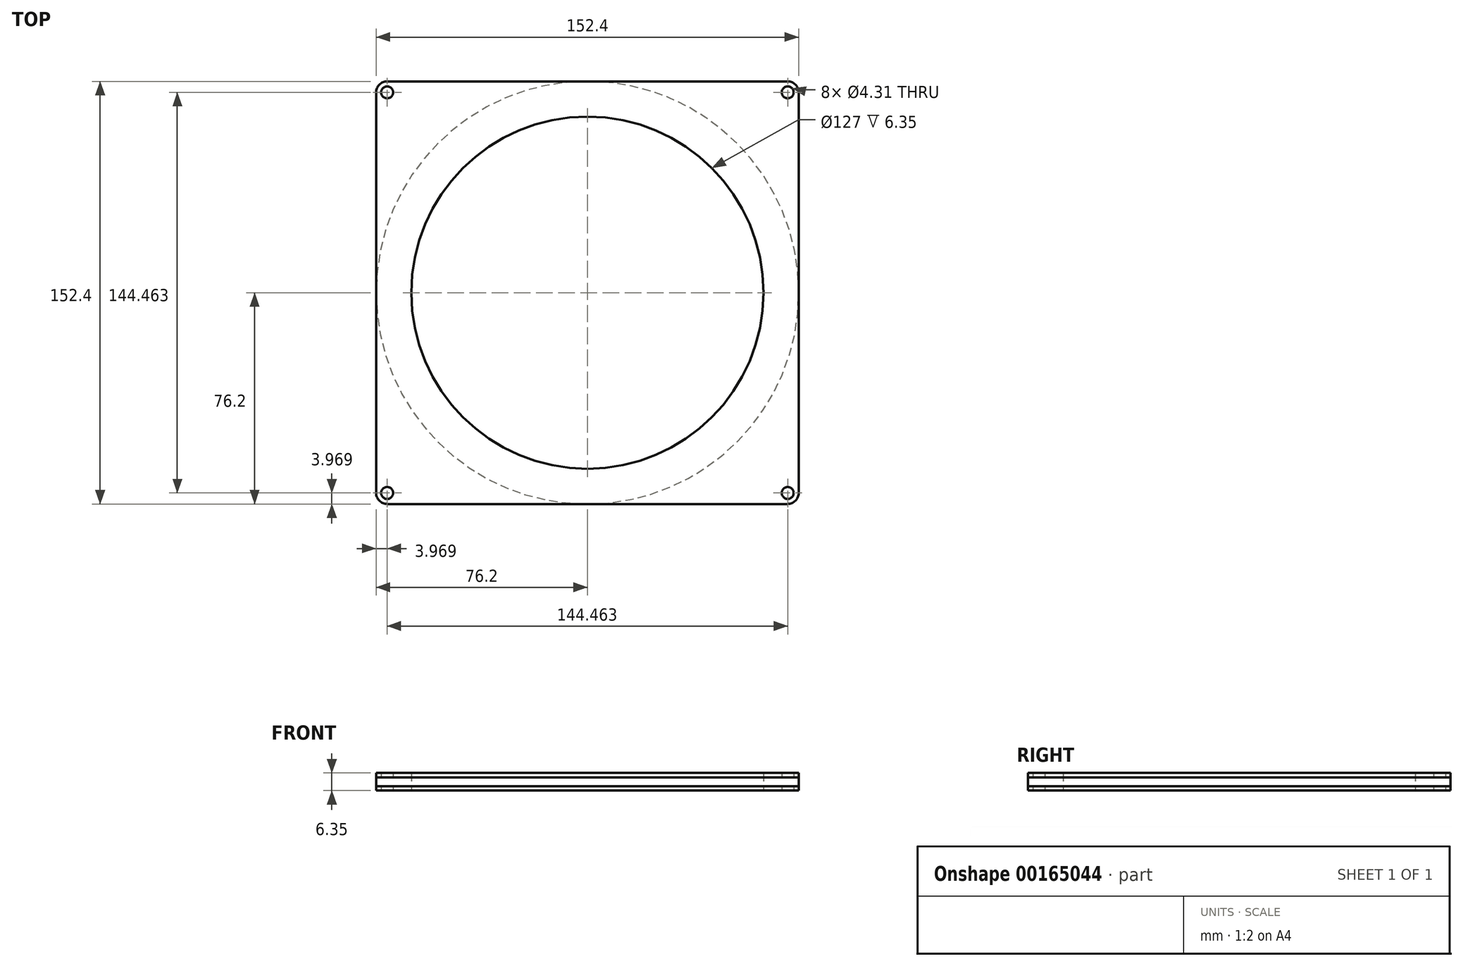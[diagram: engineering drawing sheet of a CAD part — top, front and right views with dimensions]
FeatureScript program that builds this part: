
annotation { "Feature Type Name" : "Feature", "Feature Type Description" : "" }
export const myFeature = defineFeature(function(context is Context, id is Id, definition is map)
    precondition{}
    {
        {
            var Q0;
            Q0=qCreatedBy(makeId("Top.planeOp"),FACE);
            var sketch = newSketch(context, id + "F0", { "sketchPlane" : qUnion([Q0])});
            skLineSegment(sketch, "E0.bottom", {"start": v(76.2, 76.2) * mm, "end": v(-76.2, 76.2) * mm});
            skLineSegment(sketch, "E0.top", {"start": v(76.2, -76.2) * mm, "end": v(-76.2, -76.2) * mm});
            skLineSegment(sketch, "E0.left", {"start": v(76.2, 76.2) * mm, "end": v(76.2, -76.2) * mm});
            skLineSegment(sketch, "E0.right", {"start": v(-76.2, 76.2) * mm, "end": v(-76.2, -76.2) * mm});
            skPoint(sketch, "E0.middle", {"position": v(0, 0) * mm});
            skLineSegment(sketch, "E1.bottom", {"start": v(-72.23, 72.23) * mm, "end": v(72.23, 72.23) * mm, "construction": true});
            skLineSegment(sketch, "E1.top", {"start": v(-72.23, -72.23) * mm, "end": v(72.23, -72.23) * mm, "construction": true});
            skLineSegment(sketch, "E1.left", {"start": v(-72.23, 72.23) * mm, "end": v(-72.23, -72.23) * mm, "construction": true});
            skLineSegment(sketch, "E1.right", {"start": v(72.23, 72.23) * mm, "end": v(72.23, -72.23) * mm, "construction": true});
            skLineSegment(sketch, "E2", {"start": v(0, 72.23) * mm, "end": v(0, 76.2) * mm, "construction": true});
            skCircle(sketch, "E3", {"center": v(-72.23, 72.23) * mm, "radius": 2.15 * mm});
            skCircle(sketch, "E4", {"center": v(72.23, 72.23) * mm, "radius": 2.15 * mm});
            skCircle(sketch, "E5", {"center": v(72.23, -72.23) * mm, "radius": 2.15 * mm});
            skCircle(sketch, "E6", {"center": v(-72.23, -72.23) * mm, "radius": 2.15 * mm});
            skCircle(sketch, "E7", {"center": v(0, 0) * mm, "radius": 63.5 * mm});
            skSolve(sketch);
        }
        {
            var Q0;
            Q0 = qSketchRegion(id + "F0", true);
            extrude(context, id + "F1", {"entities" : qUnion([Q0]), "depth" : 1.59 * mm});
        }
        {
            var Q0;
            Q0=makeQuery(id+"F1.opExtrude","CAP_FACE",FACE,{"disambiguationData":[OSD([sQuery(id+"F0.wireOp",EDGE,"E0.bottom"),sQuery(id+"F0.wireOp",EDGE,"E0.top"),sQuery(id+"F0.wireOp",EDGE,"E0.left"),sQuery(id+"F0.wireOp",EDGE,"E0.right"),sQuery(id+"F0.wireOp",EDGE,"E3"),sQuery(id+"F0.wireOp",EDGE,"E4"),sQuery(id+"F0.wireOp",EDGE,"E5"),sQuery(id+"F0.wireOp",EDGE,"E6")])],"isStart":false});
            var sketch = newSketch(context, id + "F2", { "sketchPlane" : qUnion([Q0])});
            skCircle(sketch, "E8", {"center": v(0, 0) * mm, "radius": 76.2 * mm});
            skCircle(sketch, "E9", {"center": v(0, 0) * mm, "radius": 63.5 * mm});
            skSolve(sketch);
        }
        {
            var Q0;
            Q0 = qSketchRegion(id + "F2", true);
            extrude(context, id + "F3", {"entities" : qUnion([Q0]), "operationType" : NewBodyOperationType.ADD, "depth" : 3.17 * mm});
        }
        {
            var Q0;
            Q0=makeQuery(id+"F3.opExtrude","CAP_FACE",FACE,{"disambiguationData":[OSD([sQuery(id+"F2.wireOp",EDGE,"E8")])],"isStart":false});
            var sketch = newSketch(context, id + "F4", { "sketchPlane" : qUnion([Q0])});
            skLineSegment(sketch, "E10.bottom", {"start": v(-76.2, -76.2) * mm, "end": v(76.2, -76.2) * mm});
            skLineSegment(sketch, "E10.top", {"start": v(-76.2, 76.2) * mm, "end": v(76.2, 76.2) * mm});
            skLineSegment(sketch, "E10.left", {"start": v(-76.2, -76.2) * mm, "end": v(-76.2, 76.2) * mm});
            skLineSegment(sketch, "E10.right", {"start": v(76.2, -76.2) * mm, "end": v(76.2, 76.2) * mm});
            skPoint(sketch, "E10.middle", {"position": v(0, 0) * mm});
            skLineSegment(sketch, "E11.bottom", {"start": v(-72.23, 72.23) * mm, "end": v(72.23, 72.23) * mm, "construction": true});
            skLineSegment(sketch, "E11.top", {"start": v(-72.23, -72.23) * mm, "end": v(72.23, -72.23) * mm, "construction": true});
            skLineSegment(sketch, "E11.left", {"start": v(-72.23, 72.23) * mm, "end": v(-72.23, -72.23) * mm, "construction": true});
            skLineSegment(sketch, "E11.right", {"start": v(72.23, 72.23) * mm, "end": v(72.23, -72.23) * mm, "construction": true});
            skCircle(sketch, "E12", {"center": v(-72.23, 72.23) * mm, "radius": 2.15 * mm});
            skCircle(sketch, "E13", {"center": v(72.23, -72.23) * mm, "radius": 2.15 * mm});
            skCircle(sketch, "E14", {"center": v(72.23, 72.23) * mm, "radius": 2.15 * mm});
            skCircle(sketch, "E15", {"center": v(-72.23, -72.23) * mm, "radius": 2.15 * mm});
            skCircle(sketch, "E16", {"center": v(0, 0) * mm, "radius": 63.5 * mm});
            skSolve(sketch);
        }
        {
            var Q0;
            Q0 = qSketchRegion(id + "F4", true);
            extrude(context, id + "F5", {"entities" : qUnion([Q0]), "operationType" : NewBodyOperationType.ADD, "depth" : 1.59 * mm});
        }
        {
            var Q0;
            Q0=makeQuery(id+"F1.opExtrude","SWEPT_EDGE",EDGE,{"disambiguationData":[OSD([sQuery(id+"F0.wireOp",EDGE,"E0.bottom"),sQuery(id+"F0.wireOp",EDGE,"E0.right")])]});
            var Q1;
            Q1=makeQuery(id+"F1.opExtrude","SWEPT_EDGE",EDGE,{"disambiguationData":[OSD([sQuery(id+"F0.wireOp",EDGE,"E0.top"),sQuery(id+"F0.wireOp",EDGE,"E0.right")])]});
            var Q2;
            Q2=makeQuery(id+"F1.opExtrude","SWEPT_EDGE",EDGE,{"disambiguationData":[OSD([sQuery(id+"F0.wireOp",EDGE,"E0.top"),sQuery(id+"F0.wireOp",EDGE,"E0.left")])]});
            var Q3;
            Q3=makeQuery(id+"F1.opExtrude","SWEPT_EDGE",EDGE,{"disambiguationData":[OSD([sQuery(id+"F0.wireOp",EDGE,"E0.bottom"),sQuery(id+"F0.wireOp",EDGE,"E0.left")])]});
            var Q4;
            Q4=makeQuery(id+"F5.opExtrude","SWEPT_EDGE",EDGE,{"disambiguationData":[OSD([sQuery(id+"F4.wireOp",EDGE,"E10.top"),sQuery(id+"F4.wireOp",EDGE,"E10.left")])]});
            var Q5;
            Q5=makeQuery(id+"F5.opExtrude","SWEPT_EDGE",EDGE,{"disambiguationData":[OSD([sQuery(id+"F4.wireOp",EDGE,"E10.bottom"),sQuery(id+"F4.wireOp",EDGE,"E10.left")])]});
            var Q6;
            Q6=makeQuery(id+"F5.opExtrude","SWEPT_EDGE",EDGE,{"disambiguationData":[OSD([sQuery(id+"F4.wireOp",EDGE,"E10.bottom"),sQuery(id+"F4.wireOp",EDGE,"E10.right")])]});
            var Q7;
            Q7=makeQuery(id+"F5.opExtrude","SWEPT_EDGE",EDGE,{"disambiguationData":[OSD([sQuery(id+"F4.wireOp",EDGE,"E10.top"),sQuery(id+"F4.wireOp",EDGE,"E10.right")])]});
            fillet(context, id + "F6", {"entities" : qUnion([Q0, Q1, Q2, Q3, Q4, Q5, Q6, Q7]), "radius" : 3.97 * mm, "tangentPropagation" : true, "allowEdgeOverflow" : false});
        }
    });
